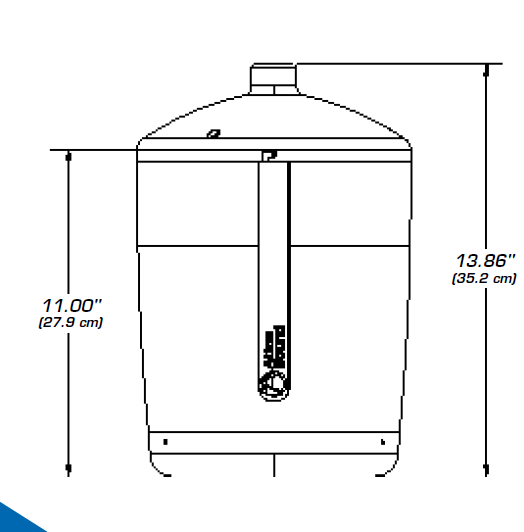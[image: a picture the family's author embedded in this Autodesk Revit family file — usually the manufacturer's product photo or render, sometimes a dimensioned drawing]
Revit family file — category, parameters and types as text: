
# Revit family: Atlas_Sound_PM4FA-WH
name_source: partatom
category: Communication Devices
units: mm (PartAtom-declared; Revit-internal decimal feet)

## family parameters
Always vertical = Yes
Cut with Voids When Loaded = No
Maintain Annotation Orientation = No
Part Type = Normal
Room Calculation Point = No
Round Connector Dimension = Use Diameter
Shared = No
Work Plane-Based = Yes

## types (1)
- Pendant Mount Loudspeaker
    100V Taps = 1, 2, 4, 8, 16 Watts and 8Ω
    70V Taps = 1, 2, 4, 8, 16 Watts and 8Ω
    Baffle Material = <By Category>
    Body Material = <By Category>
    Color = <By Category>
    Cost = 184.99 $
    Cost MSRP = 184.99 $
    Coverage Horizontal = 110.00°
    Coverage Vertical = 110.00°
    Default Elevation = 48 "
    Description = 4" 2-WAY PENDANT MOUNT LOUDSPEAKER WITH 16-WATT 70.7V TRANSFORMER - WHITE
    Dispersion Angle = 130.00°
    Enclosure Material = <By Category>
    Family Code (default) = LOUD SPEAKERS
    Frequency Response  = 70 Hz – 20 kHz (±5 dB)
    Grill Material = <By Category>
    HF Driver = Coaxially Mounted PEI Dome Tweeter
    Height = 13.86 "
    IQ Category = SPEAKERS
    Impedance = 8
    Ingress Protection = IP-21
    Manufacturer = ATLAS SOUND
    Manufacturer URL = https://www.atlasied.com
    MasterFormat = 27 41 13
    MaterFormat Title = SPEAKERS
    Model = PM4FA-WH
    Mount Material = QF_Plastic - White - Smooth
    OmniClass Number = 23-37 17 13 19
    OmniClass Title = SPEAKERS
    Power Rating (RMS) = 25 Watts @ 8 Ω
    Product Documentation Link = https://www.atlasied.com
    Product Page URL = https://www.atlasied.com
    SPL Max = 107
    ScheduleType |RF| = AtlasIED Master
    Sensitivity = 88
    Speaker Dispersion = 130.00°
    Speaker Type = S1
    Transformer Option = Yes
    URL = www.atlassound.com
    Vertical Symmetry = Yes
    Warranty = 5 Year
    Weight Product = 10
    Width = 9.26 "

## geometry (parser evidence)
native form markers: Blend x6, Sweep x2
no freeform markers — native parametric forms only
